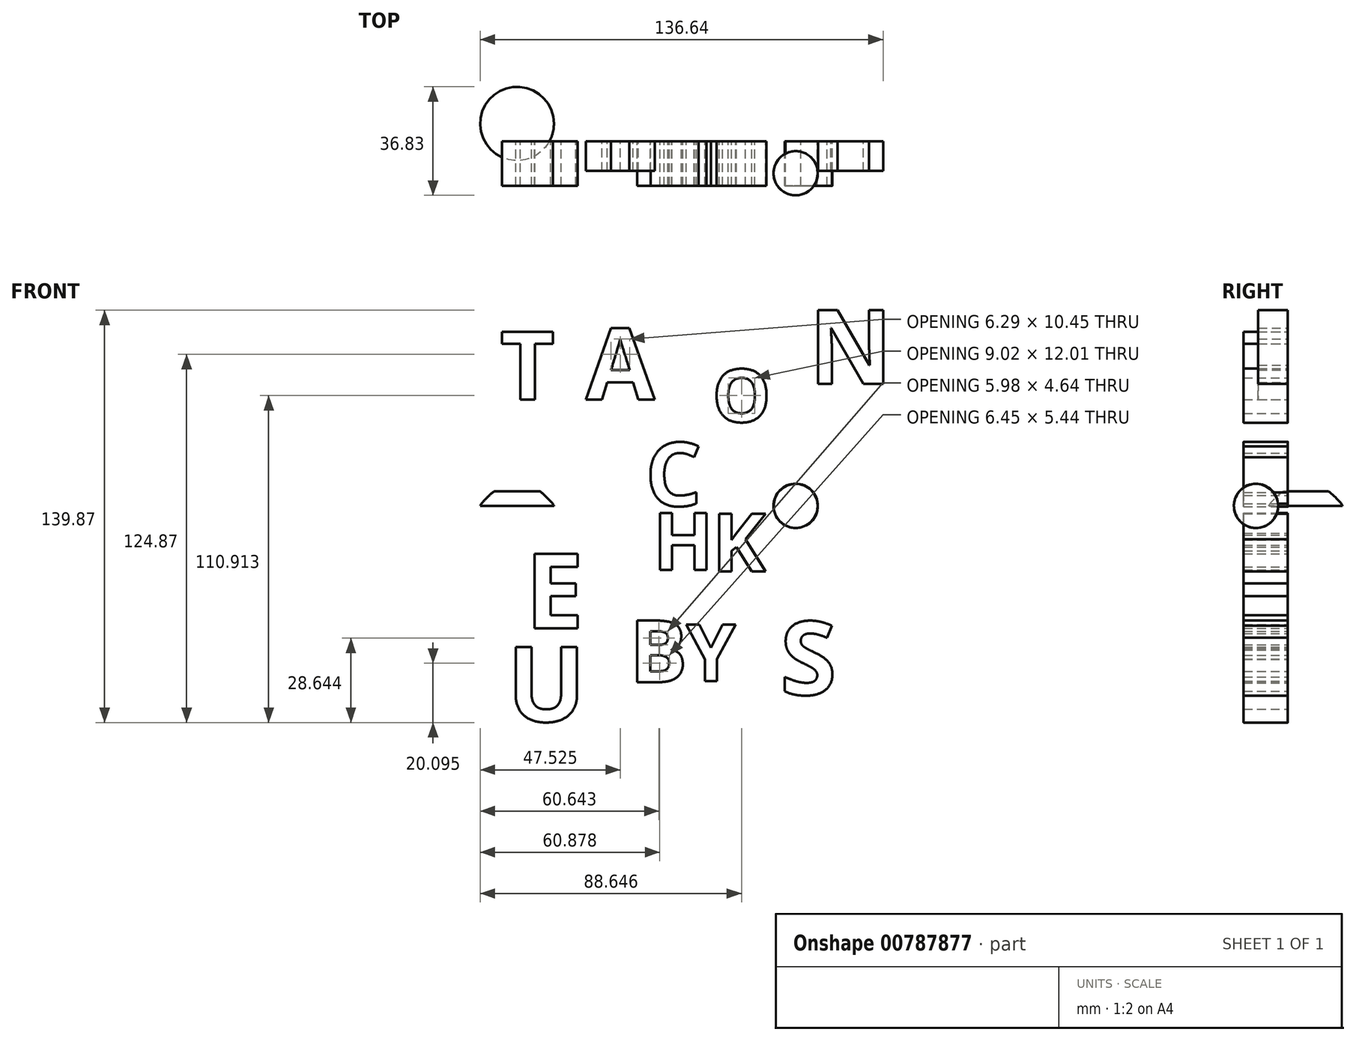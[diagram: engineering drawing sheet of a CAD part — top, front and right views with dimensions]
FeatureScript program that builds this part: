
annotation { "Feature Type Name" : "Feature", "Feature Type Description" : "" }
export const myFeature = defineFeature(function(context is Context, id is Id, definition is map)
    precondition{}
    {
        {
            var Q0;
            Q0=qCreatedBy(makeId("Front.planeOp"),FACE);
            var sketch = newSketch(context, id + "F0", { "sketchPlane" : qUnion([Q0])});
            skText(sketch, "E0", { "text": "C", "fontName": "OpenSans-Bold.ttf"});
            const initialGuessF0  = {"E0": [-0.01, 0, 1, 0, 0.0216]};
            skSetInitialGuess(sketch, initialGuessF0);
            skSolve(sketch);
        }
        {
            var Q0;
            Q0 = qSketchRegion(id + "F0", true);
            extrude(context, id + "F1", {"entities" : qUnion([Q0]), "depth" : 15 * mm, "offsetDistance" : 25 * mm});
        }
        {
            var Q0;
            Q0=qCreatedBy(makeId("Top.planeOp"),FACE);
            var sketch = newSketch(context, id + "F2", { "sketchPlane" : qUnion([Q0])});
            skCircle(sketch, "E1", {"center": v(-53.5, 6.06) * mm, "radius": 12.5 * mm});
            skSolve(sketch);
        }
        {
            var Q0;
            Q0=makeQuery(id+"F2.imprint","IMPRINT",FACE,{"disambiguationData":[TD([[makeQuery(id+"F2.imprint","IMPRINT",EDGE,{"derivedFrom":sQuery(id+"F2.wireOp",EDGE,"E1")}),1.0]])]});
            extrude(context, id + "F3", {"entities" : qUnion([Q0]), "depth" : 5 * mm, "offsetDistance" : 25 * mm});
        }
        {
            var Q0;
            Q0=makeQuery(id+"F3.opExtrude","CAP_FACE",FACE,{"disambiguationData":[OSD([sQuery(id+"F2.wireOp",EDGE,"E1")])],"isStart":false});
            var Q1;
            Q1=makeQuery(id+"F3.opExtrude","CAP_EDGE",EDGE,{"disambiguationData":[OSD([sQuery(id+"F2.wireOp",EDGE,"E1")])],"isStart":false});
            fillet(context, id + "F4", {"entities" : qUnion([Q0, Q1]), "radius" : 5 * mm, "tangentPropagation" : true, "rho" : 0.1, "crossSection" : FilletCrossSection.CONIC, "allowEdgeOverflow" : false});
        }
        {
            var Q0;
            Q0=qCreatedBy(makeId("Top.planeOp"),FACE);
            var sketch = newSketch(context, id + "F5", { "sketchPlane" : qUnion([Q0])});
            skCircle(sketch, "E2", {"center": v(40.97, -10.77) * mm, "radius": 7.5 * mm});
            skLineSegment(sketch, "E3", {"start": v(40.99, -3.27) * mm, "end": v(40.99, -18.27) * mm});
            skSolve(sketch);
        }
        {
            var Q0;
            {var subQ0=sQuery(id+"F5.wireOp",EDGE,"E3");Q0=makeQuery(id+"F5.imprint","IMPRINT",FACE,{"disambiguationData":[TD([[makeQuery(id+"F5.imprint","IMPRINT",EDGE,{"derivedFrom":subQ0}),-1.0]])]});}
            var Q1;
            Q1=sQuery(id+"F5.wireOp",EDGE,"E3");
            revolve(context, id + "F6", {"surfaceOperationType" : NewSurfaceOperationType.NEW, "entities" : qUnion([Q0]), "axis" : qUnion([Q1]), "revolveType" : RevolveType.FULL});
        }
        {
            var Q0;
            Q0=qCreatedBy(makeId("Front.planeOp"),FACE);
            var sketch = newSketch(context, id + "F7", { "sketchPlane" : qUnion([Q0])});
            skText(sketch, "E4", { "text": "H", "fontName": "OpenSans-Bold.ttf"});
            const initialGuessF7  = {"E4": [-0.0075, -0.0217, 1, 0, 0.01947]};
            skSetInitialGuess(sketch, initialGuessF7);
            skSolve(sketch);
        }
        {
            var Q0;
            Q0=makeQuery(id+"F7.imprint","IMPRINT",FACE,{"disambiguationData":[TD([[makeQuery(id+"F7.imprint","IMPRINT",EDGE,{"derivedFrom":sQuery(id+"F7.wireOp",EDGE,"E4.sketch_text.stroke-0")}),-1.0]])]});
            extrude(context, id + "F8", {"entities" : qUnion([Q0]), "depth" : 15 * mm, "offsetDistance" : 25 * mm});
        }
        {
            var Q0;
            Q0=qCreatedBy(makeId("Front.planeOp"),FACE);
            var sketch = newSketch(context, id + "F9", { "sketchPlane" : qUnion([Q0])});
            skText(sketch, "E5", { "text": "E", "fontName": "OpenSans-Bold.ttf"});
            const initialGuessF9  = {"E5": [-0.05068, -0.04156, 1, 0, 0.02545]};
            skSetInitialGuess(sketch, initialGuessF9);
            skSolve(sketch);
        }
        {
            var Q0;
            Q0=makeQuery(id+"F9.imprint","IMPRINT",FACE,{"disambiguationData":[TD([[makeQuery(id+"F9.imprint","IMPRINT",EDGE,{"derivedFrom":sQuery(id+"F9.wireOp",EDGE,"E5.sketch_text.stroke-0")}),-1.0]])]});
            extrude(context, id + "F10", {"entities" : qUnion([Q0]), "depth" : 15 * mm, "offsetDistance" : 25 * mm});
        }
        {
            var Q0;
            Q0=qCreatedBy(makeId("Front.planeOp"),FACE);
            var sketch = newSketch(context, id + "F11", { "sketchPlane" : qUnion([Q0])});
            skText(sketch, "E6", { "text": "S", "fontName": "OpenSans-Bold.ttf"});
            const initialGuessF11  = {"E6": [0.0357, -0.06406, 1, 0, 0.025]};
            skSetInitialGuess(sketch, initialGuessF11);
            skSolve(sketch);
        }
        {
            var Q0;
            Q0 = qSketchRegion(id + "F11", true);
            extrude(context, id + "F12", {"entities" : qUnion([Q0]), "depth" : 15 * mm, "offsetDistance" : 25 * mm});
        }
        {
            var Q0;
            Q0=qCreatedBy(makeId("Front.planeOp"),FACE);
            var sketch = newSketch(context, id + "F13", { "sketchPlane" : qUnion([Q0])});
            skText(sketch, "E7", { "text": "B", "fontName": "OpenSans-Bold.ttf"});
            const initialGuessF13  = {"E7": [-0.0154, -0.05978, 1, 0, 0.02105]};
            skSetInitialGuess(sketch, initialGuessF13);
            skSolve(sketch);
        }
        {
            var Q0;
            Q0 = qSketchRegion(id + "F13", true);
            extrude(context, id + "F14", {"entities" : qUnion([Q0]), "depth" : 15 * mm, "offsetDistance" : 25 * mm});
        }
        {
            var Q0;
            Q0=qCreatedBy(makeId("Front.planeOp"),FACE);
            var sketch = newSketch(context, id + "F15", { "sketchPlane" : qUnion([Q0])});
            skText(sketch, "E8", { "text": "O", "fontName": "OpenSans-Bold.ttf"});
            const initialGuessF15  = {"E8": [0.01273, 0.02849, 1, 0, 0.01794]};
            skSetInitialGuess(sketch, initialGuessF15);
            skSolve(sketch);
        }
        {
            var Q0;
            Q0 = qSketchRegion(id + "F15", true);
            extrude(context, id + "F16", {"entities" : qUnion([Q0]), "depth" : 15 * mm, "offsetDistance" : 25 * mm});
        }
        {
            var Q0;
            Q0=qCreatedBy(makeId("Front.planeOp"),FACE);
            var sketch = newSketch(context, id + "F17", { "sketchPlane" : qUnion([Q0])});
            skText(sketch, "E9", { "text": "T", "fontName": "OpenSans-Bold.ttf"});
            const initialGuessF17  = {"E9": [-0.0592, 0.03612, 1, 0, 0.02308]};
            skSetInitialGuess(sketch, initialGuessF17);
            skSolve(sketch);
        }
        {
            var Q0;
            Q0 = qSketchRegion(id + "F17", true);
            extrude(context, id + "F18", {"entities" : qUnion([Q0]), "depth" : 15 * mm, "offsetDistance" : 25 * mm});
        }
        {
            var Q0;
            Q0=qCreatedBy(makeId("Front.planeOp"),FACE);
            var sketch = newSketch(context, id + "F19", { "sketchPlane" : qUnion([Q0])});
            skText(sketch, "E10", { "text": "A", "fontName": "OpenSans-Bold.ttf"});
            const initialGuessF19  = {"E10": [-0.03017, 0.03611, 1, 0, 0.02434]};
            skSetInitialGuess(sketch, initialGuessF19);
            skSolve(sketch);
        }
        {
            var Q0;
            Q0=makeQuery(id+"F19.imprint","IMPRINT",FACE,{"disambiguationData":[TD([[makeQuery(id+"F19.imprint","IMPRINT",EDGE,{"derivedFrom":sQuery(id+"F19.wireOp",EDGE,"E10.sketch_text.stroke-0")}),-1.0]])]});
            extrude(context, id + "F20", {"entities" : qUnion([Q0]), "depth" : 10 * mm, "offsetDistance" : 25 * mm});
        }
        {
            var Q0;
            Q0=qCreatedBy(makeId("Front.planeOp"),FACE);
            var sketch = newSketch(context, id + "F21", { "sketchPlane" : qUnion([Q0])});
            skText(sketch, "E11", { "text": "N", "fontName": "OpenSans-Bold.ttf"});
            const initialGuessF21  = {"E11": [0.0454, 0.04145, 1, 0, 0.02513]};
            skSetInitialGuess(sketch, initialGuessF21);
            skSolve(sketch);
        }
        {
            var Q0;
            Q0=makeQuery(id+"F21.imprint","IMPRINT",FACE,{"disambiguationData":[TD([[makeQuery(id+"F21.imprint","IMPRINT",EDGE,{"derivedFrom":sQuery(id+"F21.wireOp",EDGE,"E11.sketch_text.stroke-0")}),-1.0]])]});
            extrude(context, id + "F22", {"entities" : qUnion([Q0]), "depth" : 10 * mm, "offsetDistance" : 25 * mm});
        }
        {
            var Q0;
            Q0=qCreatedBy(makeId("Front.planeOp"),FACE);
            var sketch = newSketch(context, id + "F23", { "sketchPlane" : qUnion([Q0])});
            skText(sketch, "E12", { "text": "K", "fontName": "OpenSans-Bold.ttf"});
            const initialGuessF23  = {"E12": [0.01256, -0.02226, 1, 0, 0.01979]};
            skSetInitialGuess(sketch, initialGuessF23);
            skSolve(sketch);
        }
        {
            var Q0;
            Q0=makeQuery(id+"F23.imprint","IMPRINT",FACE,{"disambiguationData":[TD([[makeQuery(id+"F23.imprint","IMPRINT",EDGE,{"derivedFrom":sQuery(id+"F23.wireOp",EDGE,"E12.sketch_text.stroke-0")}),-1.0]])]});
            extrude(context, id + "F24", {"entities" : qUnion([Q0]), "depth" : 15 * mm, "offsetDistance" : 25 * mm});
        }
        {
            var Q0;
            Q0=qCreatedBy(makeId("Front.planeOp"),FACE);
            var sketch = newSketch(context, id + "F25", { "sketchPlane" : qUnion([Q0])});
            skText(sketch, "E13", { "text": "Y", "fontName": "OpenSans-Bold.ttf"});
            const initialGuessF25  = {"E13": [0.00387, -0.05943, 1, 0, 0.01934]};
            skSetInitialGuess(sketch, initialGuessF25);
            skSolve(sketch);
        }
        {
            var Q0;
            Q0=makeQuery(id+"F25.imprint","IMPRINT",FACE,{"disambiguationData":[TD([[makeQuery(id+"F25.imprint","IMPRINT",EDGE,{"derivedFrom":sQuery(id+"F25.wireOp",EDGE,"E13.sketch_text.stroke-0")}),-1.0]])]});
            extrude(context, id + "F26", {"entities" : qUnion([Q0]), "depth" : 15 * mm, "offsetDistance" : 25 * mm});
        }
        {
            var Q0;
            Q0=qCreatedBy(makeId("Front.planeOp"),FACE);
            var sketch = newSketch(context, id + "F27", { "sketchPlane" : qUnion([Q0])});
            skText(sketch, "E14", { "text": "U", "fontName": "OpenSans-Bold.ttf"});
            const initialGuessF27  = {"E14": [-0.05695, -0.07315, 1, 0, 0.0255]};
            skSetInitialGuess(sketch, initialGuessF27);
            skSolve(sketch);
        }
        {
            var Q0;
            Q0=makeQuery(id+"F27.imprint","IMPRINT",FACE,{"disambiguationData":[TD([[makeQuery(id+"F27.imprint","IMPRINT",EDGE,{"derivedFrom":sQuery(id+"F27.wireOp",EDGE,"E14.sketch_text.stroke-0")}),-1.0]])]});
            extrude(context, id + "F28", {"entities" : qUnion([Q0]), "depth" : 15 * mm, "offsetDistance" : 25 * mm});
        }
    });
